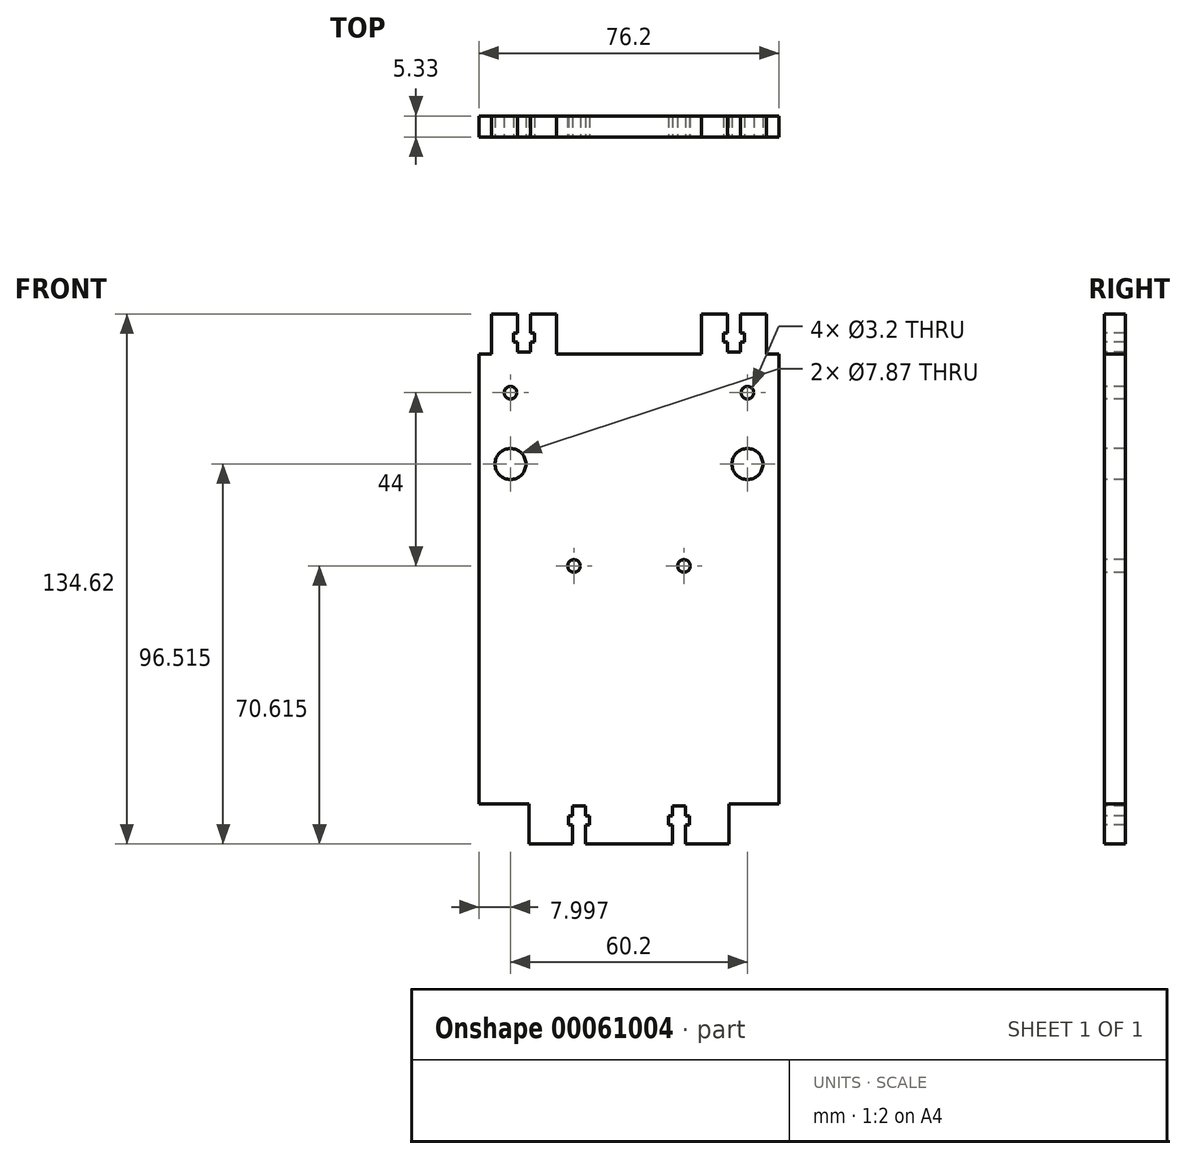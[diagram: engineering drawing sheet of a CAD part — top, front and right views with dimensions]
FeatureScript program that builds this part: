
annotation { "Feature Type Name" : "Feature", "Feature Type Description" : "" }
export const myFeature = defineFeature(function(context is Context, id is Id, definition is map)
    precondition{}
    {
        {
            var Q0;
            Q0=qCreatedBy(makeId("Front.planeOp"),FACE);
            var sketch = newSketch(context, id + "F0", { "sketchPlane" : qUnion([Q0])});
            skLineSegment(sketch, "E0.bottom", {"start": v(-26.24, 82) * mm, "end": v(49.96, 82) * mm});
            skLineSegment(sketch, "E0.top", {"start": v(-26.24, -52.61) * mm, "end": v(49.96, -52.61) * mm});
            skLineSegment(sketch, "E0.left", {"start": v(-26.24, 82) * mm, "end": v(-26.24, -52.61) * mm});
            skLineSegment(sketch, "E0.right", {"start": v(49.96, 82) * mm, "end": v(49.96, -52.61) * mm});
            skSolve(sketch);
        }
        {
            var Q0;
            Q0=makeQuery(id+"F0.imprint","IMPRINT",FACE,{"disambiguationData":[TD([[makeQuery(id+"F0.imprint","IMPRINT",EDGE,{"derivedFrom":sQuery(id+"F0.wireOp",EDGE,"E0.bottom")}),-1.0]])]});
            extrude(context, id + "F1", {"entities" : qUnion([Q0]), "depth" : 5.33 * mm});
        }
        {
            var Q0;
            Q0=makeQuery(id+"F1.opExtrude","CAP_FACE",FACE,{"disambiguationData":[OSD([sQuery(id+"F0.wireOp",EDGE,"E0.bottom"),sQuery(id+"F0.wireOp",EDGE,"E0.top"),sQuery(id+"F0.wireOp",EDGE,"E0.left"),sQuery(id+"F0.wireOp",EDGE,"E0.right")])],"isStart":false});
            var sketch = newSketch(context, id + "F2", { "sketchPlane" : qUnion([Q0])});
            skLineSegment(sketch, "E1.bottom", {"start": v(-26.24, -52.61) * mm, "end": v(-13.54, -52.61) * mm});
            skLineSegment(sketch, "E1.top", {"start": v(-26.24, -42.45) * mm, "end": v(-13.54, -42.45) * mm});
            skLineSegment(sketch, "E1.left", {"start": v(-26.24, -52.61) * mm, "end": v(-26.24, -42.45) * mm});
            skLineSegment(sketch, "E1.right", {"start": v(-13.54, -52.61) * mm, "end": v(-13.54, -42.45) * mm});
            skLineSegment(sketch, "E2.bottom", {"start": v(49.96, -52.61) * mm, "end": v(37.26, -52.61) * mm});
            skLineSegment(sketch, "E2.top", {"start": v(49.96, -42.45) * mm, "end": v(37.26, -42.45) * mm});
            skLineSegment(sketch, "E2.left", {"start": v(49.96, -52.61) * mm, "end": v(49.96, -42.45) * mm});
            skLineSegment(sketch, "E2.right", {"start": v(37.26, -52.61) * mm, "end": v(37.26, -42.45) * mm});
            skSolve(sketch);
        }
        {
            var Q0;
            Q0=makeQuery(id+"F2.imprint","IMPRINT",FACE,{"disambiguationData":[TD([[makeQuery(id+"F2.imprint","IMPRINT",EDGE,{"derivedFrom":sQuery(id+"F2.wireOp",EDGE,"E1.bottom")}),1.0]])]});
            var Q1;
            Q1=makeQuery(id+"F2.imprint","IMPRINT",FACE,{"disambiguationData":[TD([[makeQuery(id+"F2.imprint","IMPRINT",EDGE,{"derivedFrom":sQuery(id+"F2.wireOp",EDGE,"E2.bottom")}),1.0]])]});
            extrude(context, id + "F3", {"entities" : qUnion([Q0, Q1]), "operationType" : NewBodyOperationType.REMOVE, "oppositeDirection" : true, "depth" : 25.4 * mm});
        }
        {
            var Q0;
            Q0=makeQuery(id+"F1.opExtrude","CAP_FACE",FACE,{"disambiguationData":[OSD([sQuery(id+"F0.wireOp",EDGE,"E0.bottom"),sQuery(id+"F0.wireOp",EDGE,"E0.top"),sQuery(id+"F0.wireOp",EDGE,"E0.left"),sQuery(id+"F0.wireOp",EDGE,"E0.right")])],"isStart":false});
            var sketch = newSketch(context, id + "F4", { "sketchPlane" : qUnion([Q0])});
            skLineSegment(sketch, "E3.bottom", {"start": v(-2.5, -52.61) * mm, "end": v(0.8, -52.61) * mm});
            skLineSegment(sketch, "E3.top", {"start": v(-2.5, -42.96) * mm, "end": v(0.8, -42.96) * mm});
            skLineSegment(sketch, "E3.left", {"start": v(-2.5, -52.61) * mm, "end": v(-2.5, -42.96) * mm});
            skLineSegment(sketch, "E3.right", {"start": v(0.8, -52.61) * mm, "end": v(0.8, -42.96) * mm});
            skLineSegment(sketch, "E4.bottom", {"start": v(-3.54, -45.5) * mm, "end": v(1.85, -45.5) * mm});
            skLineSegment(sketch, "E4.top", {"start": v(-3.54, -47.79) * mm, "end": v(1.85, -47.79) * mm});
            skLineSegment(sketch, "E4.left", {"start": v(-3.54, -45.5) * mm, "end": v(-3.54, -47.79) * mm});
            skLineSegment(sketch, "E4.right", {"start": v(1.85, -45.5) * mm, "end": v(1.85, -47.79) * mm});
            skLineSegment(sketch, "E5", {"start": v(11.86, -52.61) * mm, "end": v(11.86, -40.08) * mm});
            skLineSegment(sketch, "E6.MirrorCS", {"start": v(21.86, -45.5) * mm, "end": v(21.86, -47.79) * mm});
            skLineSegment(sketch, "E7.MirrorCS", {"start": v(22.9, -52.61) * mm, "end": v(22.9, -42.96) * mm});
            skLineSegment(sketch, "E8.MirrorCS", {"start": v(26.2, -42.96) * mm, "end": v(22.9, -42.96) * mm});
            skLineSegment(sketch, "E9.MirrorCS", {"start": v(26.2, -52.61) * mm, "end": v(26.2, -42.96) * mm});
            skLineSegment(sketch, "E10.MirrorCS", {"start": v(27.25, -45.5) * mm, "end": v(27.25, -47.79) * mm});
            skLineSegment(sketch, "E11.MirrorCS", {"start": v(27.25, -45.5) * mm, "end": v(21.86, -45.5) * mm});
            skLineSegment(sketch, "E12.MirrorCS", {"start": v(27.25, -47.79) * mm, "end": v(21.86, -47.79) * mm});
            skLineSegment(sketch, "E13.MirrorCS", {"start": v(26.2, -52.61) * mm, "end": v(22.9, -52.61) * mm});
            skSolve(sketch);
        }
        {
            var Q0;
            {var subQ0=sQuery(id+"F4.wireOp",EDGE,"E3.bottom");Q0=makeQuery(id+"F4.imprint","IMPRINT",FACE,{"disambiguationData":[TD([[makeQuery(id+"F4.imprint","IMPRINT",EDGE,{"derivedFrom":subQ0}),1.0]])]});}
            var Q1;
            {var subQ0=sQuery(id+"F4.wireOp",EDGE,"E4.top");var subQ1=sQuery(id+"F4.wireOp",EDGE,"E3.left");var subQ2=makeQuery(id+"F4.imprint","INTERSECT",VERTEX,{"derivedFrom":[subQ1,subQ0]});Q1=makeQuery(id+"F4.imprint","IMPRINT",FACE,{"disambiguationData":[TD([[makeQuery(id+"F4.imprint","IMPRINT",EDGE,{"disambiguationData":[TD([[subQ2,-1.0]])],"derivedFrom":subQ1}),-1.0]])]});}
            var Q2;
            {var subQ5=sQuery(id+"F4.wireOp",EDGE,"E4.left");Q2=makeQuery(id+"F4.imprint","IMPRINT",FACE,{"disambiguationData":[TD([[makeQuery(id+"F4.imprint","IMPRINT",EDGE,{"derivedFrom":subQ5}),1.0]])]});}
            var Q3;
            {var subQ0=sQuery(id+"F4.wireOp",EDGE,"E3.top");Q3=makeQuery(id+"F4.imprint","IMPRINT",FACE,{"disambiguationData":[TD([[makeQuery(id+"F4.imprint","IMPRINT",EDGE,{"derivedFrom":subQ0}),-1.0]])]});}
            var Q4;
            {var subQ5=sQuery(id+"F4.wireOp",EDGE,"E4.right");Q4=makeQuery(id+"F4.imprint","IMPRINT",FACE,{"disambiguationData":[TD([[makeQuery(id+"F4.imprint","IMPRINT",EDGE,{"derivedFrom":subQ5}),-1.0]])]});}
            var Q5;
            {var subQ0=sQuery(id+"F4.wireOp",EDGE,"E13.MirrorCS");Q5=makeQuery(id+"F4.imprint","IMPRINT",FACE,{"disambiguationData":[TD([[makeQuery(id+"F4.imprint","IMPRINT",EDGE,{"derivedFrom":subQ0}),1.0]])]});}
            var Q6;
            {var subQ0=sQuery(id+"F4.wireOp",EDGE,"E12.MirrorCS");var subQ1=sQuery(id+"F4.wireOp",EDGE,"E7.MirrorCS");var subQ2=makeQuery(id+"F4.imprint","INTERSECT",VERTEX,{"derivedFrom":[subQ1,subQ0]});Q6=makeQuery(id+"F4.imprint","IMPRINT",FACE,{"disambiguationData":[TD([[makeQuery(id+"F4.imprint","IMPRINT",EDGE,{"disambiguationData":[TD([[subQ2,-1.0]])],"derivedFrom":subQ1}),-1.0]])]});}
            var Q7;
            {var subQ0=sQuery(id+"F4.wireOp",EDGE,"E6.MirrorCS");Q7=makeQuery(id+"F4.imprint","IMPRINT",FACE,{"disambiguationData":[TD([[makeQuery(id+"F4.imprint","IMPRINT",EDGE,{"derivedFrom":subQ0}),1.0]])]});}
            var Q8;
            {var subQ5=sQuery(id+"F4.wireOp",EDGE,"E10.MirrorCS");Q8=makeQuery(id+"F4.imprint","IMPRINT",FACE,{"disambiguationData":[TD([[makeQuery(id+"F4.imprint","IMPRINT",EDGE,{"derivedFrom":subQ5}),-1.0]])]});}
            var Q9;
            {var subQ0=sQuery(id+"F4.wireOp",EDGE,"E8.MirrorCS");Q9=makeQuery(id+"F4.imprint","IMPRINT",FACE,{"disambiguationData":[TD([[makeQuery(id+"F4.imprint","IMPRINT",EDGE,{"derivedFrom":subQ0}),1.0]])]});}
            extrude(context, id + "F5", {"entities" : qUnion([Q0, Q1, Q2, Q3, Q4, Q5, Q6, Q7, Q8, Q9]), "operationType" : NewBodyOperationType.REMOVE, "oppositeDirection" : true, "depth" : 25.4 * mm});
        }
        {
            var Q0;
            Q0=makeQuery(id+"F1.opExtrude","CAP_FACE",FACE,{"disambiguationData":[OSD([sQuery(id+"F0.wireOp",EDGE,"E0.bottom"),sQuery(id+"F0.wireOp",EDGE,"E0.top"),sQuery(id+"F0.wireOp",EDGE,"E0.left"),sQuery(id+"F0.wireOp",EDGE,"E0.right")])],"isStart":false});
            var sketch = newSketch(context, id + "F6", { "sketchPlane" : qUnion([Q0])});
            skLineSegment(sketch, "E14.bottom", {"start": v(-26.24, 82) * mm, "end": v(-23.07, 82) * mm});
            skLineSegment(sketch, "E14.top", {"start": v(-26.24, 71.85) * mm, "end": v(-23.07, 71.85) * mm});
            skLineSegment(sketch, "E14.left", {"start": v(-26.24, 82) * mm, "end": v(-26.24, 71.85) * mm});
            skLineSegment(sketch, "E14.right", {"start": v(-23.07, 82) * mm, "end": v(-23.07, 71.85) * mm});
            skLineSegment(sketch, "E15.bottom", {"start": v(49.96, 82) * mm, "end": v(46.78, 82) * mm});
            skLineSegment(sketch, "E15.top", {"start": v(49.96, 71.85) * mm, "end": v(46.78, 71.85) * mm});
            skLineSegment(sketch, "E15.left", {"start": v(49.96, 82) * mm, "end": v(49.96, 71.85) * mm});
            skLineSegment(sketch, "E15.right", {"start": v(46.78, 82) * mm, "end": v(46.78, 71.85) * mm});
            skLineSegment(sketch, "E16.bottom", {"start": v(-6.56, 82) * mm, "end": v(30.27, 82) * mm});
            skLineSegment(sketch, "E16.top", {"start": v(-6.56, 71.85) * mm, "end": v(30.27, 71.85) * mm});
            skLineSegment(sketch, "E16.left", {"start": v(-6.56, 82) * mm, "end": v(-6.56, 71.85) * mm});
            skLineSegment(sketch, "E16.right", {"start": v(30.27, 82) * mm, "end": v(30.27, 71.85) * mm});
            skSolve(sketch);
        }
        {
            var Q0;
            Q0=makeQuery(id+"F6.imprint","IMPRINT",FACE,{"disambiguationData":[TD([[makeQuery(id+"F6.imprint","IMPRINT",EDGE,{"derivedFrom":sQuery(id+"F6.wireOp",EDGE,"E14.bottom")}),-1.0]])]});
            var Q1;
            Q1=makeQuery(id+"F6.imprint","IMPRINT",FACE,{"disambiguationData":[TD([[makeQuery(id+"F6.imprint","IMPRINT",EDGE,{"derivedFrom":sQuery(id+"F6.wireOp",EDGE,"E16.bottom")}),-1.0]])]});
            var Q2;
            Q2=makeQuery(id+"F6.imprint","IMPRINT",FACE,{"disambiguationData":[TD([[makeQuery(id+"F6.imprint","IMPRINT",EDGE,{"derivedFrom":sQuery(id+"F6.wireOp",EDGE,"E15.bottom")}),-1.0]])]});
            extrude(context, id + "F7", {"entities" : qUnion([Q0, Q1, Q2]), "operationType" : NewBodyOperationType.REMOVE, "oppositeDirection" : true, "depth" : 25.4 * mm});
        }
        {
            var Q0;
            Q0=makeQuery(id+"F1.opExtrude","CAP_FACE",FACE,{"disambiguationData":[OSD([sQuery(id+"F0.wireOp",EDGE,"E0.bottom"),sQuery(id+"F0.wireOp",EDGE,"E0.top"),sQuery(id+"F0.wireOp",EDGE,"E0.left"),sQuery(id+"F0.wireOp",EDGE,"E0.right")])],"isStart":false});
            var sketch = newSketch(context, id + "F8", { "sketchPlane" : qUnion([Q0])});
            skLineSegment(sketch, "E17.bottom", {"start": v(-16.46, 82) * mm, "end": v(-13.16, 82) * mm});
            skLineSegment(sketch, "E17.top", {"start": v(-16.46, 72.35) * mm, "end": v(-13.16, 72.35) * mm});
            skLineSegment(sketch, "E17.left", {"start": v(-16.46, 82) * mm, "end": v(-16.46, 72.35) * mm});
            skLineSegment(sketch, "E17.right", {"start": v(-13.16, 82) * mm, "end": v(-13.16, 72.35) * mm});
            skLineSegment(sketch, "E18.bottom", {"start": v(-17.5, 77.18) * mm, "end": v(-12.12, 77.18) * mm});
            skLineSegment(sketch, "E18.top", {"start": v(-17.5, 74.9) * mm, "end": v(-12.12, 74.9) * mm});
            skLineSegment(sketch, "E18.left", {"start": v(-17.5, 77.18) * mm, "end": v(-17.5, 74.9) * mm});
            skLineSegment(sketch, "E18.right", {"start": v(-12.12, 77.18) * mm, "end": v(-12.12, 74.9) * mm});
            skLineSegment(sketch, "E19.MirrorCS", {"start": v(40.18, 72.35) * mm, "end": v(36.88, 72.35) * mm});
            skLineSegment(sketch, "E20.MirrorCS", {"start": v(40.18, 82) * mm, "end": v(40.18, 72.35) * mm});
            skLineSegment(sketch, "E21.MirrorCS", {"start": v(36.88, 82) * mm, "end": v(36.88, 72.35) * mm});
            skLineSegment(sketch, "E22.MirrorCS", {"start": v(41.22, 74.9) * mm, "end": v(35.83, 74.9) * mm});
            skLineSegment(sketch, "E23.MirrorCS", {"start": v(41.22, 77.18) * mm, "end": v(41.22, 74.9) * mm});
            skLineSegment(sketch, "E24.MirrorCS", {"start": v(41.22, 77.18) * mm, "end": v(35.83, 77.18) * mm});
            skLineSegment(sketch, "E25.MirrorCS", {"start": v(35.83, 77.18) * mm, "end": v(35.83, 74.9) * mm});
            skLineSegment(sketch, "E26.MirrorCS", {"start": v(40.18, 82) * mm, "end": v(36.88, 82) * mm});
            skSolve(sketch);
        }
        {
            var Q0;
            {var subQ0=sQuery(id+"F8.wireOp",EDGE,"E17.bottom");Q0=makeQuery(id+"F8.imprint","IMPRINT",FACE,{"disambiguationData":[TD([[makeQuery(id+"F8.imprint","IMPRINT",EDGE,{"derivedFrom":subQ0}),-1.0]])]});}
            var Q1;
            {var subQ0=sQuery(id+"F8.wireOp",EDGE,"E18.bottom");var subQ1=sQuery(id+"F8.wireOp",EDGE,"E17.left");var subQ2=makeQuery(id+"F8.imprint","INTERSECT",VERTEX,{"derivedFrom":[subQ1,subQ0]});Q1=makeQuery(id+"F8.imprint","IMPRINT",FACE,{"disambiguationData":[TD([[makeQuery(id+"F8.imprint","IMPRINT",EDGE,{"disambiguationData":[TD([[subQ2,-1.0]])],"derivedFrom":subQ1}),1.0]])]});}
            var Q2;
            {var subQ0=sQuery(id+"F8.wireOp",EDGE,"E17.top");Q2=makeQuery(id+"F8.imprint","IMPRINT",FACE,{"disambiguationData":[TD([[makeQuery(id+"F8.imprint","IMPRINT",EDGE,{"derivedFrom":subQ0}),1.0]])]});}
            var Q3;
            {var subQ5=sQuery(id+"F8.wireOp",EDGE,"E18.left");Q3=makeQuery(id+"F8.imprint","IMPRINT",FACE,{"disambiguationData":[TD([[makeQuery(id+"F8.imprint","IMPRINT",EDGE,{"derivedFrom":subQ5}),1.0]])]});}
            var Q4;
            {var subQ5=sQuery(id+"F8.wireOp",EDGE,"E18.right");Q4=makeQuery(id+"F8.imprint","IMPRINT",FACE,{"disambiguationData":[TD([[makeQuery(id+"F8.imprint","IMPRINT",EDGE,{"derivedFrom":subQ5}),-1.0]])]});}
            var Q5;
            {var subQ0=sQuery(id+"F8.wireOp",EDGE,"E19.MirrorCS");Q5=makeQuery(id+"F8.imprint","IMPRINT",FACE,{"disambiguationData":[TD([[makeQuery(id+"F8.imprint","IMPRINT",EDGE,{"derivedFrom":subQ0}),-1.0]])]});}
            var Q6;
            {var subQ0=sQuery(id+"F8.wireOp",EDGE,"E24.MirrorCS");var subQ1=sQuery(id+"F8.wireOp",EDGE,"E20.MirrorCS");var subQ2=makeQuery(id+"F8.imprint","INTERSECT",VERTEX,{"derivedFrom":[subQ1,subQ0]});Q6=makeQuery(id+"F8.imprint","IMPRINT",FACE,{"disambiguationData":[TD([[makeQuery(id+"F8.imprint","IMPRINT",EDGE,{"disambiguationData":[TD([[subQ2,-1.0]])],"derivedFrom":subQ1}),-1.0]])]});}
            var Q7;
            {var subQ5=sQuery(id+"F8.wireOp",EDGE,"E25.MirrorCS");Q7=makeQuery(id+"F8.imprint","IMPRINT",FACE,{"disambiguationData":[TD([[makeQuery(id+"F8.imprint","IMPRINT",EDGE,{"derivedFrom":subQ5}),1.0]])]});}
            var Q8;
            {var subQ5=sQuery(id+"F8.wireOp",EDGE,"E23.MirrorCS");Q8=makeQuery(id+"F8.imprint","IMPRINT",FACE,{"disambiguationData":[TD([[makeQuery(id+"F8.imprint","IMPRINT",EDGE,{"derivedFrom":subQ5}),-1.0]])]});}
            var Q9;
            {var subQ0=sQuery(id+"F8.wireOp",EDGE,"E26.MirrorCS");Q9=makeQuery(id+"F8.imprint","IMPRINT",FACE,{"disambiguationData":[TD([[makeQuery(id+"F8.imprint","IMPRINT",EDGE,{"derivedFrom":subQ0}),-1.0]])]});}
            extrude(context, id + "F9", {"entities" : qUnion([Q0, Q1, Q2, Q3, Q4, Q5, Q6, Q7, Q8, Q9]), "operationType" : NewBodyOperationType.REMOVE, "oppositeDirection" : true, "depth" : 25.4 * mm});
        }
        {
            var Q0;
            Q0=makeQuery(id+"F1.opExtrude","CAP_FACE",FACE,{"disambiguationData":[OSD([sQuery(id+"F0.wireOp",EDGE,"E0.bottom"),sQuery(id+"F0.wireOp",EDGE,"E0.top"),sQuery(id+"F0.wireOp",EDGE,"E0.left"),sQuery(id+"F0.wireOp",EDGE,"E0.right")])],"isStart":false});
            var sketch = newSketch(context, id + "F10", { "sketchPlane" : qUnion([Q0])});
            skCircle(sketch, "E27", {"center": v(-18.24, 62) * mm, "radius": 1.6 * mm});
            skCircle(sketch, "E28", {"center": v(41.96, 62) * mm, "radius": 1.6 * mm});
            skCircle(sketch, "E29", {"center": v(-18.24, 43.9) * mm, "radius": 3.94 * mm});
            skPoint(sketch, "E30.orphan", {"position": v(-42.02, 44) * mm});
            skCircle(sketch, "E31", {"center": v(41.96, 43.9) * mm, "radius": 3.94 * mm});
            skCircle(sketch, "E32", {"center": v(-2.11, 18) * mm, "radius": 1.6 * mm});
            skCircle(sketch, "E33", {"center": v(25.83, 18) * mm, "radius": 1.6 * mm});
            skSolve(sketch);
        }
        {
            var Q0;
            Q0 = qSketchRegion(id + "F10", true);
            extrude(context, id + "F11", {"entities" : qUnion([Q0]), "operationType" : NewBodyOperationType.REMOVE, "oppositeDirection" : true, "depth" : 25.4 * mm});
        }
    });
